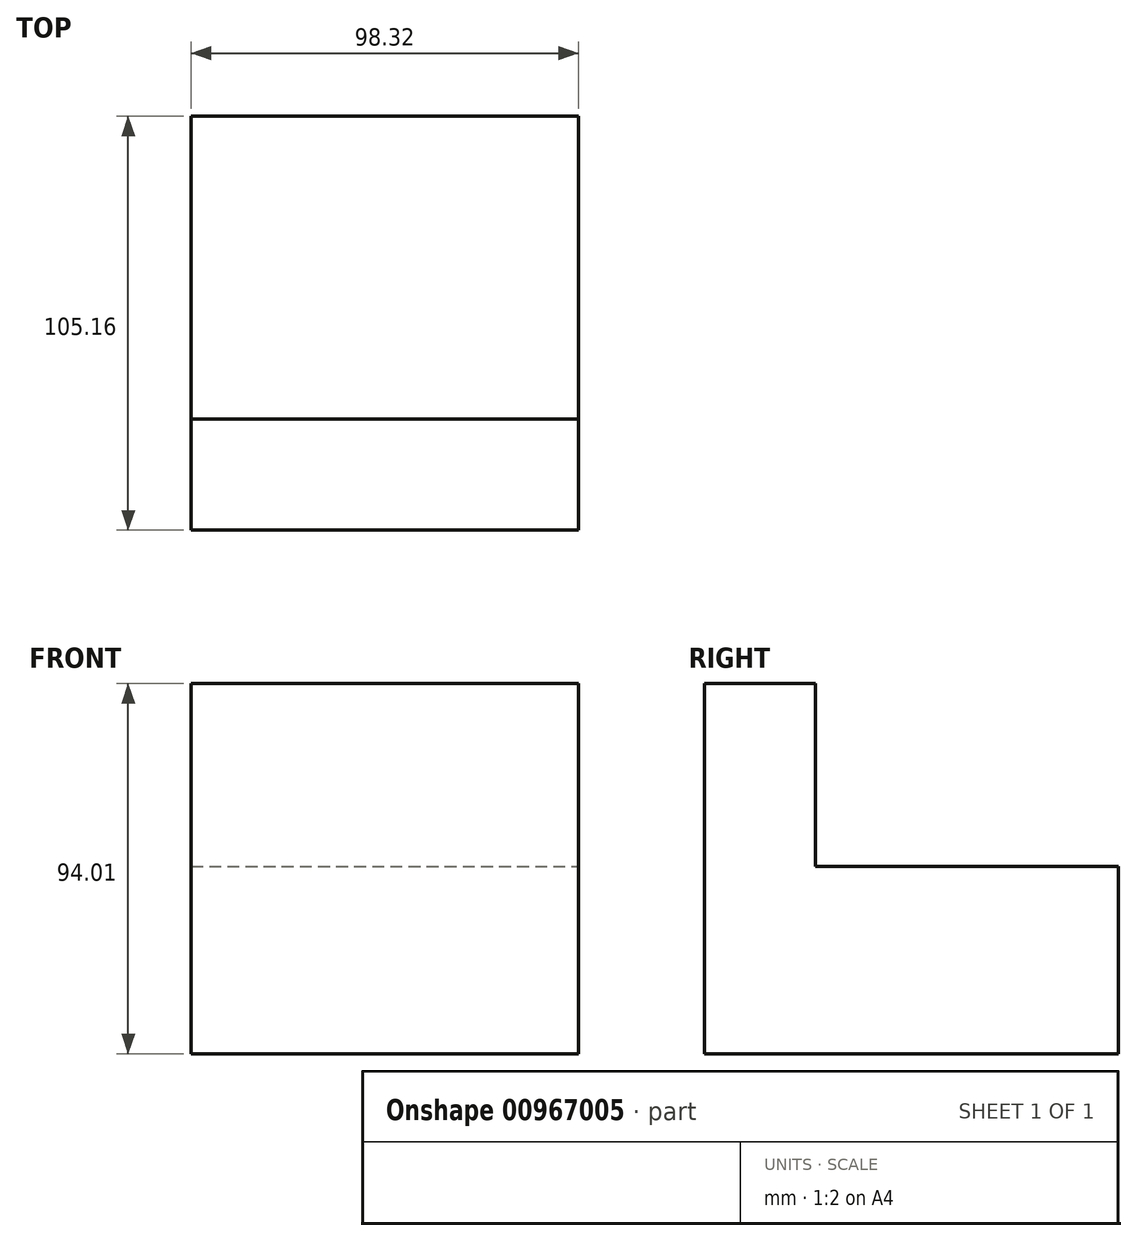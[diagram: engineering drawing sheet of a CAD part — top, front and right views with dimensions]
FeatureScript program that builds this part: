
annotation { "Feature Type Name" : "Feature", "Feature Type Description" : "" }
export const myFeature = defineFeature(function(context is Context, id is Id, definition is map)
    precondition{}
    {
        {
            var Q0;
            Q0=qCreatedBy(makeId("Front.planeOp"),FACE);
            var sketch = newSketch(context, id + "F0", { "sketchPlane" : qUnion([Q0])});
            skLineSegment(sketch, "E0.bottom", {"start": v(-49.79, 0) * mm, "end": v(48.53, 0) * mm});
            skLineSegment(sketch, "E0.top", {"start": v(-49.79, 47.53) * mm, "end": v(48.53, 47.53) * mm});
            skLineSegment(sketch, "E0.left", {"start": v(-49.79, 0) * mm, "end": v(-49.79, 47.53) * mm});
            skLineSegment(sketch, "E0.right", {"start": v(48.53, 0) * mm, "end": v(48.53, 47.53) * mm});
            skSolve(sketch);
        }
        {
            var Q0;
            Q0 = qSketchRegion(id + "F0", true);
            var Q1;
            Q1=makeQuery(id+"F0.imprint","IMPRINT",FACE,{"disambiguationData":[TD([[makeQuery(id+"F0.imprint","IMPRINT",EDGE,{"derivedFrom":sQuery(id+"F0.wireOp",EDGE,"E0.bottom")}),1.0]])]});
            extrude(context, id + "F1", {"entities" : qUnion([Q0, Q1]), "depth" : 105.16 * mm, "offsetDistance" : 25.4 * mm});
        }
        {
            var Q0;
            Q0=makeQuery(id+"F1.opExtrude","SWEPT_FACE",FACE,{"disambiguationData":[OSD([sQuery(id+"F0.wireOp",EDGE,"E0.top")])]});
            var sketch = newSketch(context, id + "F2", { "sketchPlane" : qUnion([Q0])});
            skLineSegment(sketch, "E1", {"start": v(-49.79, -76.95) * mm, "end": v(48.53, -76.95) * mm});
            skSolve(sketch);
        }
        {
            var Q0;
            {var subQ0=sQuery(id+"F2.wireOp",EDGE,"E1");Q0=makeQuery(id+"F2.imprint","IMPRINT",FACE,{"disambiguationData":[TD([[makeQuery(id+"F2.imprint","IMPRINT",EDGE,{"derivedFrom":subQ0}),-1.0]])]});}
            extrude(context, id + "F3", {"entities" : qUnion([Q0]), "operationType" : NewBodyOperationType.ADD, "depth" : 46.48 * mm, "offsetDistance" : 25.4 * mm});
        }
    });
